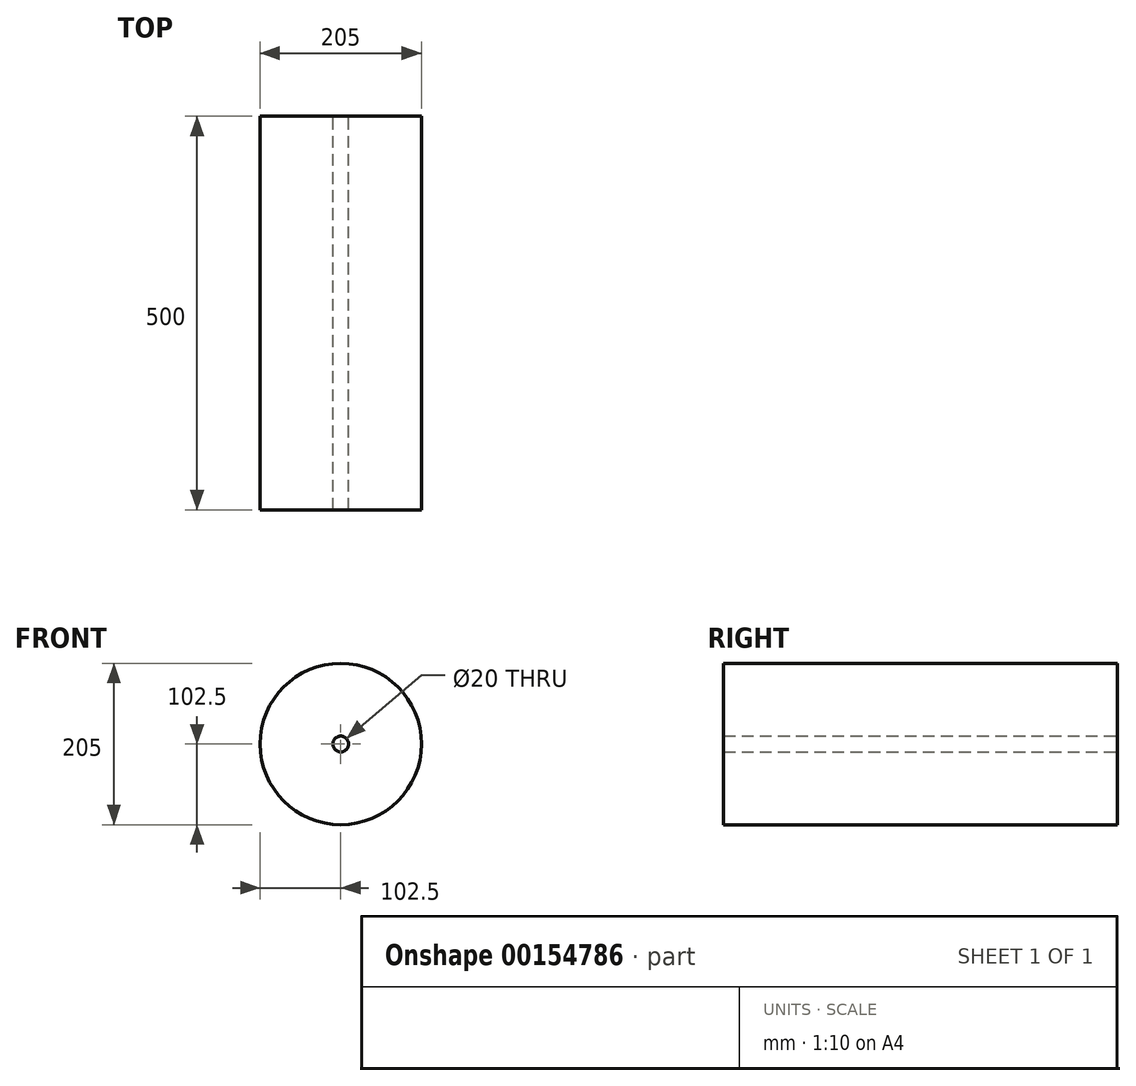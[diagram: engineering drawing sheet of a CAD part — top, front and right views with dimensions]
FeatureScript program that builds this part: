
annotation { "Feature Type Name" : "Feature", "Feature Type Description" : "" }
export const myFeature = defineFeature(function(context is Context, id is Id, definition is map)
    precondition{}
    {
        {
            var Q0;
            Q0=qCreatedBy(makeId("Front.planeOp"),FACE);
            var sketch = newSketch(context, id + "F0", { "sketchPlane" : qUnion([Q0])});
            skCircle(sketch, "E0", {"center": v(0, 0) * mm, "radius": 102.5 * mm});
            skCircle(sketch, "E1", {"center": v(0, 0) * mm, "radius": 10 * mm});
            skSolve(sketch);
        }
        {
            var Q0;
            Q0=qSketchRegion(id+"F0",true);
            extrude(context, id + "F1", {"entities" : qUnion([Q0]), "depth" : 500 * mm});
        }
    });
